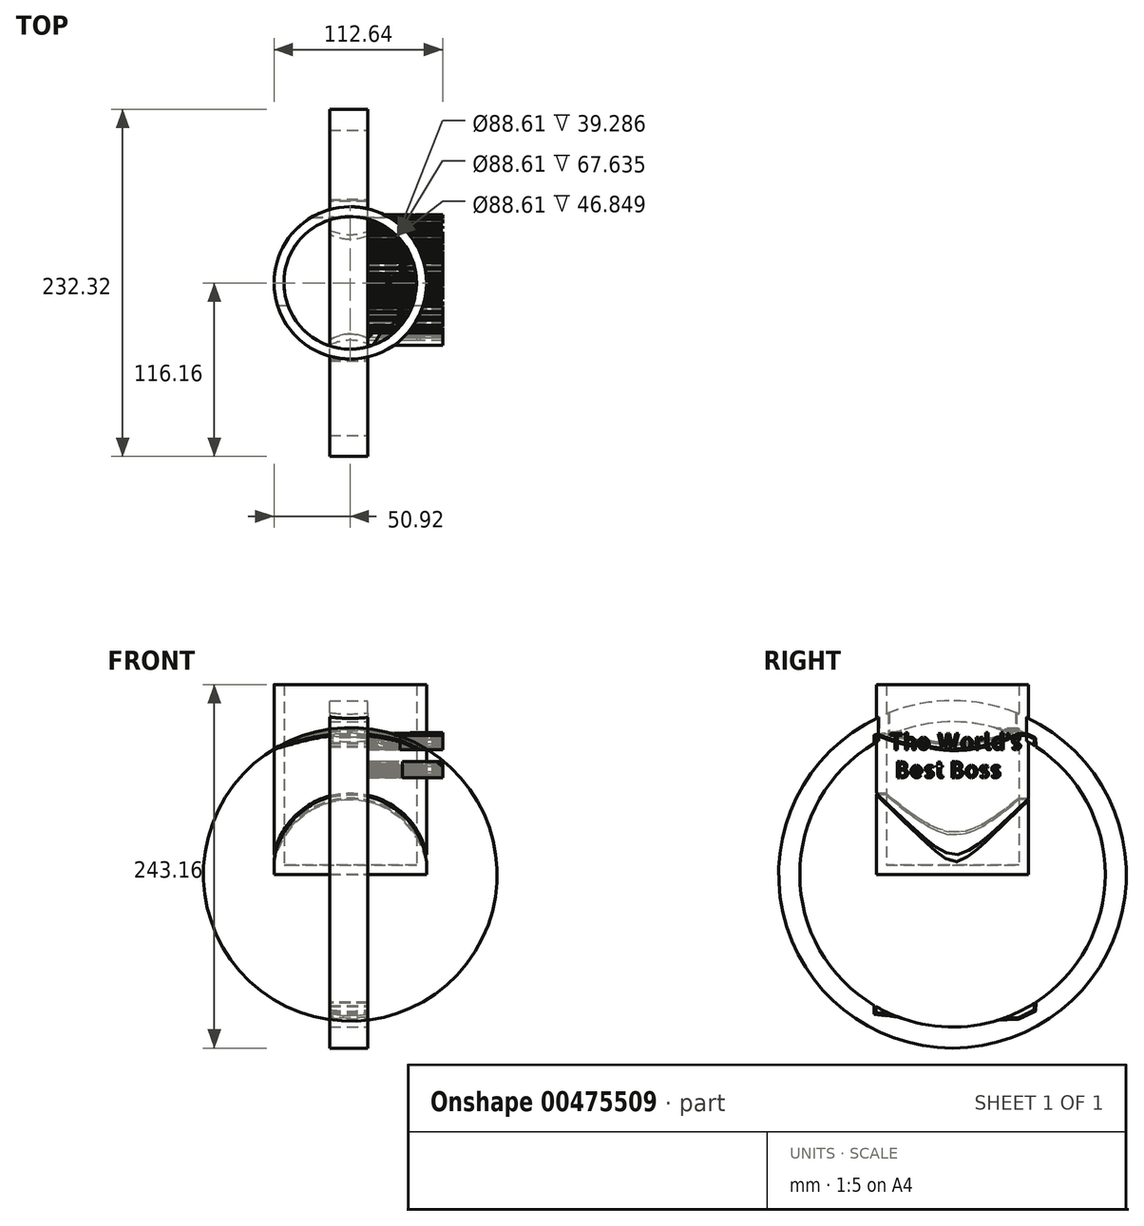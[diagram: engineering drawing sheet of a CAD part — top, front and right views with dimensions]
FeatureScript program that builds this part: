
annotation { "Feature Type Name" : "Feature", "Feature Type Description" : "" }
export const myFeature = defineFeature(function(context is Context, id is Id, definition is map)
    precondition{}
    {
        {
            var Q0;
            Q0=qCreatedBy(makeId("Top.planeOp"),FACE);
            var sketch = newSketch(context, id + "F0", { "sketchPlane" : qUnion([Q0])});
            skCircle(sketch, "E0", {"center": v(0, 0) * mm, "radius": 50.92 * mm});
            skCircle(sketch, "E1", {"center": v(0, 0) * mm, "radius": 44.3 * mm});
            skSolve(sketch);
        }
        {
            var Q0;
            Q0 = qSketchRegion(id + "F0", true);
            extrude(context, id + "F1", {"entities" : qUnion([Q0]), "depth" : 127 * mm});
        }
        {
            var Q0;
            Q0=qCreatedBy(makeId("Top.planeOp"),FACE);
            var sketch = newSketch(context, id + "F2", { "sketchPlane" : qUnion([Q0])});
            skCircle(sketch, "E2", {"center": v(0, 0) * mm, "radius": 50.8 * mm});
            skSolve(sketch);
        }
        {
            var Q0;
            Q0 = qSketchRegion(id + "F2", true);
            extrude(context, id + "F3", {"entities" : qUnion([Q0]), "operationType" : NewBodyOperationType.ADD, "depth" : 6.35 * mm});
        }
        {
            var Q0;
            Q0=qCreatedBy(makeId("Front.planeOp"),FACE);
            var sketch = newSketch(context, id + "F4", { "sketchPlane" : qUnion([Q0])});
            skLineSegment(sketch, "E3.bottom", {"start": v(11.72, 116.16) * mm, "end": v(-13.8, 116.16) * mm});
            skLineSegment(sketch, "E3.top", {"start": v(11.72, 102.1) * mm, "end": v(-13.8, 102.1) * mm});
            skLineSegment(sketch, "E3.left", {"start": v(11.72, 116.16) * mm, "end": v(11.72, 102.1) * mm});
            skLineSegment(sketch, "E3.right", {"start": v(-13.8, 116.16) * mm, "end": v(-13.8, 102.1) * mm});
            skLineSegment(sketch, "E4", {"start": v(0, 0) * mm, "end": v(-96.1, 0) * mm, "construction": true});
            skLineSegment(sketch, "E5", {"start": v(0, 0) * mm, "end": v(0, -88.93) * mm, "construction": true});
            skSolve(sketch);
        }
        {
            var Q0;
            Q0 = qSketchRegion(id + "F4", true);
            var Q1;
            Q1=sQuery(id+"F4.wireOp",EDGE,"E4");
            revolve(context, id + "F5", {"operationType" : NewBodyOperationType.ADD, "entities" : qUnion([Q0]), "axis" : qUnion([Q1]), "revolveType" : RevolveType.FULL});
        }
        {
            var Q0;
            Q0=makeQuery(id+"F5.boolean.opBoolean","SPLIT",FACE,{"disambiguationData":[TD([makeQuery(id+"F1.opExtrude","SWEPT_FACE",FACE,{"disambiguationData":[OSD([sQuery(id+"F0.wireOp",EDGE,"E1")])]})])],"derivedFrom":makeQuery(id+"F5.opRevolve","SWEPT_FACE",FACE,{"disambiguationData":[OSD([sQuery(id+"F4.wireOp",EDGE,"E3.left")])]})});
            var sketch = newSketch(context, id + "F6", { "sketchPlane" : qUnion([Q0])});
            skText(sketch, "E6", { "text": "The World\'s\n Best Boss\n", "fontName": "AllertaStencil-Regular.ttf"});
            const initialGuessF6  = {"E6": [-0.04231, 0.08356, 1, 0, 0.01057]};
            skSetInitialGuess(sketch, initialGuessF6);
            skSolve(sketch);
        }
        {
            var Q0;
            Q0 = qSketchRegion(id + "F6", true);
            extrude(context, id + "F7", {"entities" : qUnion([Q0]), "operationType" : NewBodyOperationType.ADD, "depth" : 50 * mm});
        }
        {
            var Q0;
            Q0=qCreatedBy(makeId("Right.planeOp"),FACE);
            var sketch = newSketch(context, id + "F8", { "sketchPlane" : qUnion([Q0])});
            skLineSegment(sketch, "E7", {"start": v(43.67, 96.69) * mm, "end": v(54.6, 91.4) * mm});
            skLineSegment(sketch, "E8", {"start": v(54.6, 91.4) * mm, "end": v(56.71, 50.64) * mm});
            skLineSegment(sketch, "E9", {"start": v(56.71, 50.64) * mm, "end": v(-51.29, 54.44) * mm});
            skLineSegment(sketch, "E10", {"start": v(-51.29, 54.44) * mm, "end": v(-51.29, 93.17) * mm});
            skLineSegment(sketch, "E11", {"start": v(-51.29, 93.17) * mm, "end": v(-15.08, 97.48) * mm});
            skLineSegment(sketch, "E12", {"start": v(-15.08, 97.48) * mm, "end": v(43.67, 96.69) * mm});
            skLineSegment(sketch, "E13", {"start": v(0, 0) * mm, "end": v(83.83, 0) * mm, "construction": true});
            skLineSegment(sketch, "E14.0", {"start": v(55.6, 91.46) * mm, "end": v(57.71, 50.69) * mm});
            skLineSegment(sketch, "E15.0", {"start": v(-15.13, 98.48) * mm, "end": v(43.9, 97.68) * mm});
            skLineSegment(sketch, "E15.1", {"start": v(55.58, 92.05) * mm, "end": v(57.77, 49.6) * mm});
            skLineSegment(sketch, "E15.2", {"start": v(57.77, 49.6) * mm, "end": v(-52.29, 53.48) * mm});
            skLineSegment(sketch, "E15.3", {"start": v(43.9, 97.68) * mm, "end": v(55.58, 92.05) * mm});
            skLineSegment(sketch, "E15.4", {"start": v(-52.29, 53.48) * mm, "end": v(-52.29, 94.06) * mm});
            skLineSegment(sketch, "E15.5", {"start": v(-52.29, 94.06) * mm, "end": v(-15.13, 98.48) * mm});
            skSolve(sketch);
        }
        {
            var Q0;
            Q0 = qSketchRegion(id + "F8", true);
            var Q1;
            Q1=sQuery(id+"F8.wireOp",EDGE,"E13");
            revolve(context, id + "F9", {"operationType" : NewBodyOperationType.REMOVE, "entities" : qUnion([Q0]), "axis" : qUnion([Q1]), "revolveType" : RevolveType.FULL, "oppositeDirection" : true});
        }
    });
